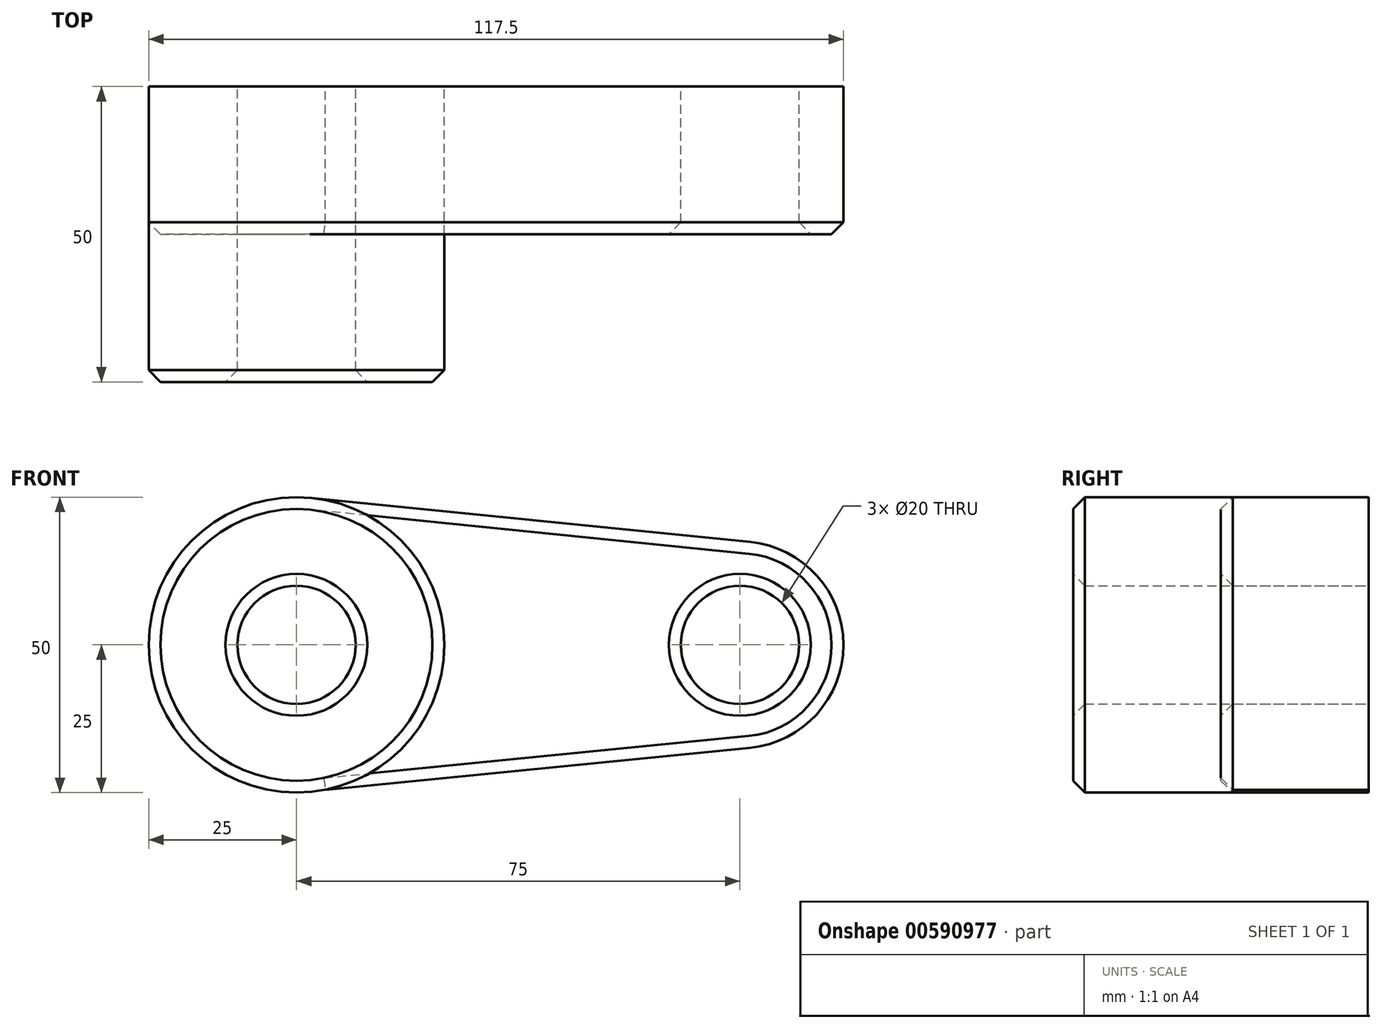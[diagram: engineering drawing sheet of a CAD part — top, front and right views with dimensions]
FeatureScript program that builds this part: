
annotation { "Feature Type Name" : "Feature", "Feature Type Description" : "" }
export const myFeature = defineFeature(function(context is Context, id is Id, definition is map)
    precondition{}
    {
        {
            var Q0;
            Q0=qCreatedBy(makeId("Front.planeOp"),FACE);
            var sketch = newSketch(context, id + "F0", { "sketchPlane" : qUnion([Q0])});
            skCircle(sketch, "E0", {"center": v(0, 0) * mm, "radius": 25 * mm});
            skCircle(sketch, "E1", {"center": v(75, 0) * mm, "radius": 17.5 * mm});
            skCircle(sketch, "E2", {"center": v(0, 0) * mm, "radius": 10 * mm});
            skCircle(sketch, "E3", {"center": v(75, 0) * mm, "radius": 10 * mm});
            skLineSegment(sketch, "E4", {"start": v(0, 25) * mm, "end": v(75, 17.59) * mm, "construction": true});
            skLineSegment(sketch, "E5", {"start": v(0, -25) * mm, "end": v(76.72, -17.42) * mm, "construction": true});
            skLineSegment(sketch, "E6", {"start": v(2.5, 24.87) * mm, "end": v(76.75, 17.41) * mm});
            skLineSegment(sketch, "E7", {"start": v(4.9, -24.52) * mm, "end": v(76.72, -17.42) * mm});
            skSolve(sketch);
        }
        {
            var Q0;
            Q0=makeQuery(id+"F0.imprint","IMPRINT",FACE,{"disambiguationData":[TD([[makeQuery(id+"F0.imprint","IMPRINT",EDGE,{"derivedFrom":sQuery(id+"F0.wireOp",EDGE,"E3")}),-1.0]])]});
            var Q1;
            Q1=makeQuery(id+"F0.imprint","IMPRINT",FACE,{"disambiguationData":[TD([[makeQuery(id+"F0.imprint","IMPRINT",EDGE,{"derivedFrom":sQuery(id+"F0.wireOp",EDGE,"E2")}),-1.0]])]});
            var Q2;
            {var subQ0=sQuery(id+"F0.wireOp",EDGE,"E6");Q2=makeQuery(id+"F0.imprint","IMPRINT",FACE,{"disambiguationData":[TD([[makeQuery(id+"F0.imprint","IMPRINT",EDGE,{"derivedFrom":subQ0}),-1.0]])]});}
            extrude(context, id + "F1", {"entities" : qUnion([Q0, Q1, Q2]), "depth" : 25 * mm, "offsetDistance" : 25.4 * mm});
        }
        {
            var Q0;
            Q0=makeQuery(id+"F0.imprint","IMPRINT",FACE,{"disambiguationData":[TD([[makeQuery(id+"F0.imprint","IMPRINT",EDGE,{"derivedFrom":sQuery(id+"F0.wireOp",EDGE,"E2")}),-1.0]])]});
            extrude(context, id + "F2", {"entities" : qUnion([Q0]), "depth" : 50 * mm, "offsetDistance" : 25.4 * mm});
        }
        {
            var Q0;
            Q0=makeQuery(id+"F2.opExtrude","CAP_EDGE",EDGE,{"disambiguationData":[OSD([sQuery(id+"F0.wireOp",EDGE,"E0")])],"isStart":false});
            var Q1;
            Q1=makeQuery(id+"F2.opExtrude","CAP_EDGE",EDGE,{"disambiguationData":[OSD([sQuery(id+"F0.wireOp",EDGE,"E2")])],"isStart":false});
            var Q2;
            Q2=makeQuery(id+"F1.opExtrude","CAP_EDGE",EDGE,{"disambiguationData":[OSD([sQuery(id+"F0.wireOp",EDGE,"E3")])],"isStart":false});
            var Q3;
            Q3=makeQuery(id+"F1.opExtrude","CAP_EDGE",EDGE,{"disambiguationData":[OSD([sQuery(id+"F0.wireOp",EDGE,"E1")])],"isStart":false});
            chamfer(context, id + "F3", {"entities" : qUnion([Q0, Q1, Q2, Q3]), "width" : 2 * mm, "tangentPropagation" : true});
        }
    });
